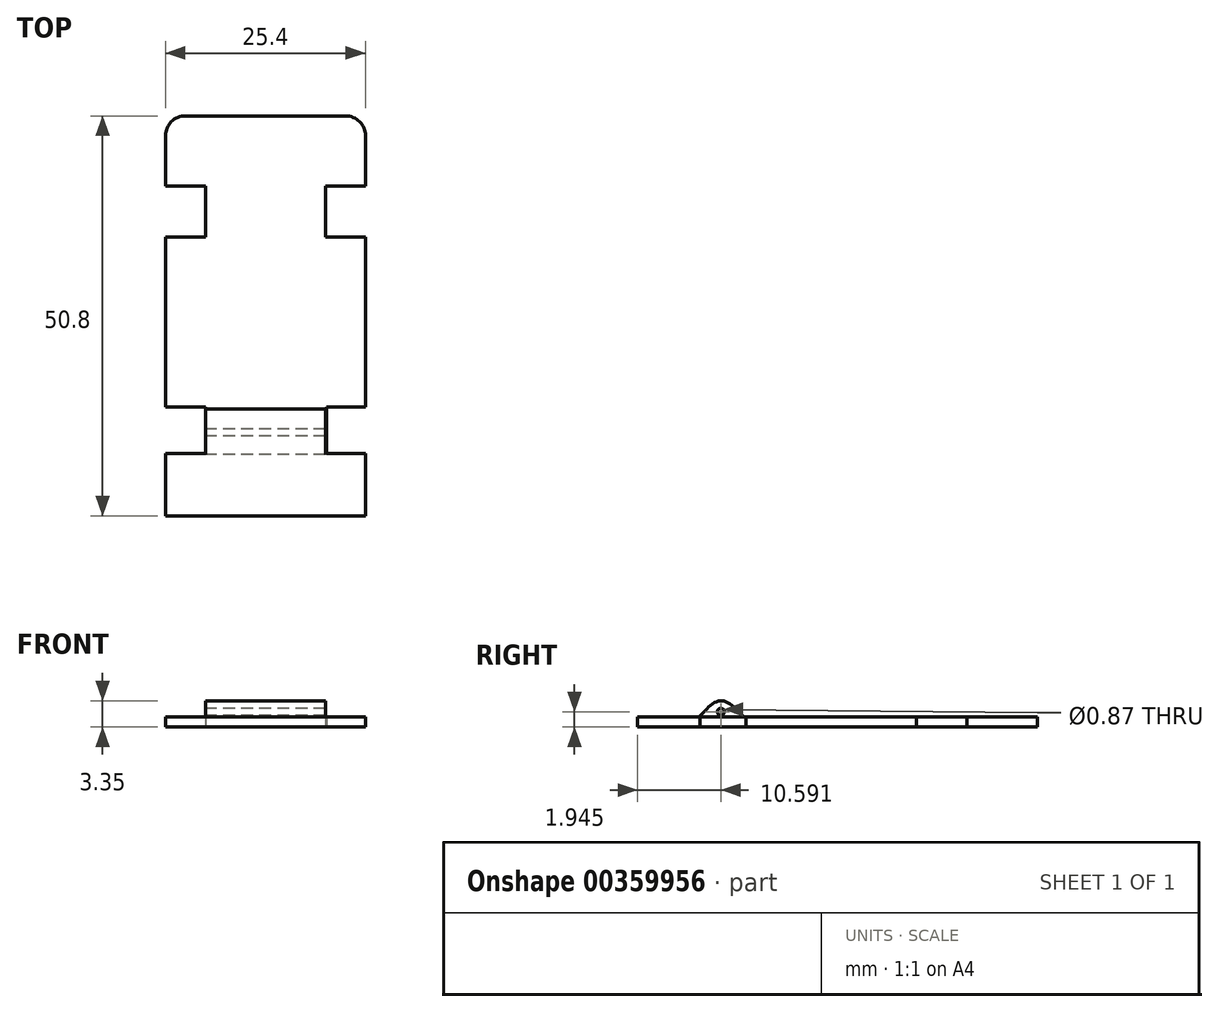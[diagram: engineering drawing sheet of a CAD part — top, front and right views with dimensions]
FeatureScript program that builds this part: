
annotation { "Feature Type Name" : "Feature", "Feature Type Description" : "" }
export const myFeature = defineFeature(function(context is Context, id is Id, definition is map)
    precondition{}
    {
        {
            var Q0;
            Q0=qCreatedBy(makeId("Top.planeOp"),FACE);
            var sketch = newSketch(context, id + "F0", { "sketchPlane" : qUnion([Q0])});
            skPoint(sketch, "E0.middle", {"position": v(0, 0) * mm});
            skLineSegment(sketch, "E1.bottom", {"start": v(10.16, 25.4) * mm, "end": v(-10.16, 25.4) * mm});
            skLineSegment(sketch, "E1.top", {"start": v(12.7, -25.4) * mm, "end": v(-12.7, -25.4) * mm});
            skLineSegment(sketch, "E1.left", {"start": v(12.7, 22.86) * mm, "end": v(12.7, 16.48) * mm});
            skLineSegment(sketch, "E1.right", {"start": v(-12.7, 22.86) * mm, "end": v(-12.7, 16.48) * mm});
            skLineSegment(sketch, "E2", {"start": v(-12.7, 16.48) * mm, "end": v(-7.62, 16.48) * mm});
            skLineSegment(sketch, "E3", {"start": v(-7.62, 16.48) * mm, "end": v(-7.62, 10.02) * mm});
            skLineSegment(sketch, "E4", {"start": v(-7.62, 10.02) * mm, "end": v(-12.7, 10.02) * mm});
            skLineSegment(sketch, "E5.MirrorCS", {"start": v(12.7, 16.48) * mm, "end": v(7.62, 16.48) * mm});
            skLineSegment(sketch, "E6.MirrorCS", {"start": v(7.62, 16.48) * mm, "end": v(7.62, 10.02) * mm});
            skLineSegment(sketch, "E7.MirrorCS", {"start": v(7.62, 10.02) * mm, "end": v(12.7, 10.02) * mm});
            skLineSegment(sketch, "E8", {"start": v(-12.7, -11.6) * mm, "end": v(-7.62, -11.6) * mm});
            skLineSegment(sketch, "E9", {"start": v(-7.62, -11.6) * mm, "end": v(-7.62, -17.5) * mm});
            skLineSegment(sketch, "E10", {"start": v(-7.62, -17.5) * mm, "end": v(-12.7, -17.5) * mm});
            skLineSegment(sketch, "E11", {"start": v(12.7, -11.6) * mm, "end": v(7.79, -11.6) * mm});
            skLineSegment(sketch, "E12", {"start": v(7.79, -11.6) * mm, "end": v(7.79, -17.5) * mm});
            skLineSegment(sketch, "E13", {"start": v(7.79, -17.5) * mm, "end": v(12.7, -17.5) * mm});
            skLineSegment(sketch, "E14.trimOffspring", {"start": v(-12.7, 10.02) * mm, "end": v(-12.7, -11.6) * mm});
            skLineSegment(sketch, "E15.trimOffspring", {"start": v(12.7, 10.02) * mm, "end": v(12.7, -11.6) * mm});
            skLineSegment(sketch, "E16.trimOffspring", {"start": v(12.7, -17.5) * mm, "end": v(12.7, -25.4) * mm});
            skLineSegment(sketch, "E17.trimOffspring", {"start": v(-12.7, -17.5) * mm, "end": v(-12.7, -25.4) * mm});
            skPoint(sketch, "E18.visualSharp", {"position": v(-12.7, 25.4) * mm});
            skArc(sketch, "E18.filletArc", {"start": v(-10.16, 25.4) * mm, "mid": v(-11.96, 24.66) * mm, "end": v(-12.7, 22.86) * mm});
            skPoint(sketch, "E19.visualSharp", {"position": v(12.7, 25.4) * mm});
            skArc(sketch, "E19.filletArc", {"start": v(12.7, 22.86) * mm, "mid": v(11.96, 24.66) * mm, "end": v(10.16, 25.4) * mm});
            skSolve(sketch);
        }
        {
            var Q0;
            Q0=makeQuery(id+"F0.imprint","IMPRINT",FACE,{"disambiguationData":[TD([[makeQuery(id+"F0.imprint","IMPRINT",EDGE,{"derivedFrom":sQuery(id+"F0.wireOp",EDGE,"E1.bottom")}),1.0]])]});
            extrude(context, id + "F1", {"entities" : qUnion([Q0]), "depth" : 1.27 * mm});
        }
        {
            var Q0;
            Q0=qCreatedBy(makeId("Right.planeOp"),FACE);
            var sketch = newSketch(context, id + "F2", { "sketchPlane" : qUnion([Q0])});
            skFitSpline(sketch, "E20", {"points": [v(-17.64, 1.19) * mm, v(-14.8, 3.35) * mm, v(-11.85, 1.27) * mm], "startDerivative": vector(5.64, 6.47) * mm, "endDerivative": vector(5.96, -6.28) * mm});
            skLineSegment(sketch, "E21", {"start": v(-17.64, 1.19) * mm, "end": v(-11.85, 1.27) * mm});
            skCircle(sketch, "E22", {"center": v(-14.8, 1.94) * mm, "radius": 0.44 * mm});
            skSolve(sketch);
        }
        {
            var Q0;
            Q0=makeQuery(id+"F2.imprint","IMPRINT",FACE,{"disambiguationData":[TD([[makeQuery(id+"F2.imprint","IMPRINT",EDGE,{"derivedFrom":sQuery(id+"F2.wireOp",EDGE,"E20")}),-1.0]])]});
            extrude(context, id + "F3", {"entities" : qUnion([Q0]), "endBound" : BoundingType.SYMMETRIC, "depth" : 15.24 * mm});
        }
    });
